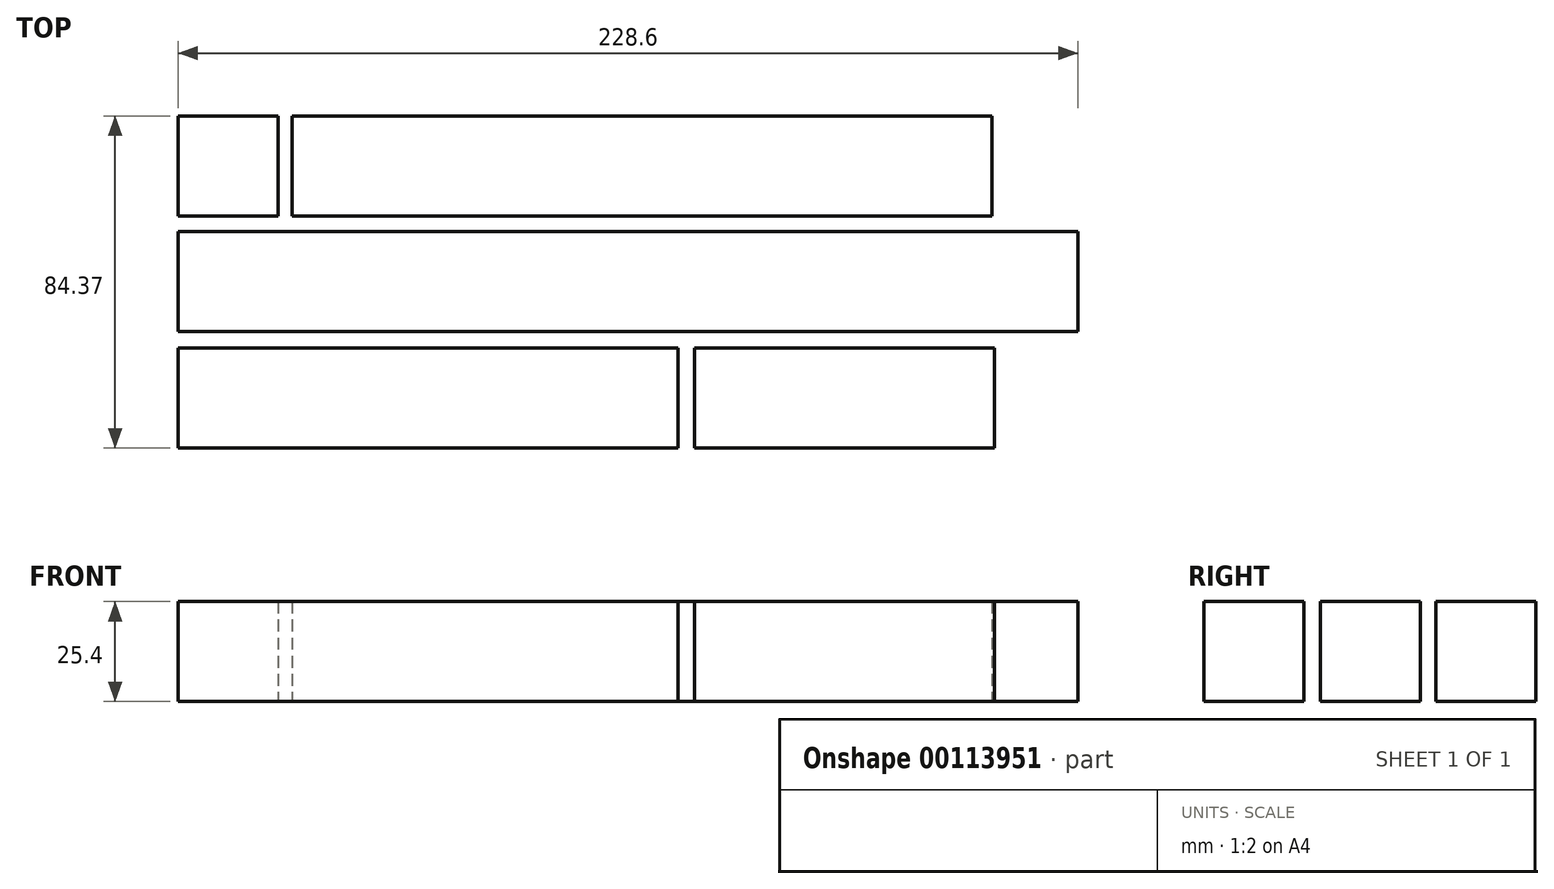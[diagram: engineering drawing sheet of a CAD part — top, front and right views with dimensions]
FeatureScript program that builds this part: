
annotation { "Feature Type Name" : "Feature", "Feature Type Description" : "" }
export const myFeature = defineFeature(function(context is Context, id is Id, definition is map)
    precondition{}
    {
        {
            var Q0;
            Q0=qCreatedBy(makeId("Top.planeOp"),FACE);
            var sketch = newSketch(context, id + "F0", { "sketchPlane" : qUnion([Q0])});
            skLineSegment(sketch, "E0.bottom", {"start": v(-116.9, 54.77) * mm, "end": v(-91.5, 54.77) * mm});
            skLineSegment(sketch, "E0.top", {"start": v(-116.9, 29.37) * mm, "end": v(-91.5, 29.37) * mm});
            skLineSegment(sketch, "E0.left", {"start": v(-116.9, 54.77) * mm, "end": v(-116.9, 29.37) * mm});
            skLineSegment(sketch, "E0.right", {"start": v(-91.5, 54.77) * mm, "end": v(-91.5, 29.37) * mm});
            skLineSegment(sketch, "E1.bottom", {"start": v(-116.9, 25.4) * mm, "end": v(111.7, 25.4) * mm});
            skLineSegment(sketch, "E1.top", {"start": v(-116.9, 0) * mm, "end": v(111.7, 0) * mm});
            skLineSegment(sketch, "E1.left", {"start": v(-116.9, 25.4) * mm, "end": v(-116.9, 0) * mm});
            skLineSegment(sketch, "E1.right", {"start": v(111.7, 25.4) * mm, "end": v(111.7, 0) * mm});
            skLineSegment(sketch, "E2.bottom", {"start": v(-87.91, 54.77) * mm, "end": v(89.89, 54.77) * mm});
            skLineSegment(sketch, "E2.top", {"start": v(-87.91, 29.37) * mm, "end": v(89.89, 29.37) * mm});
            skLineSegment(sketch, "E2.left", {"start": v(-87.91, 54.77) * mm, "end": v(-87.91, 29.37) * mm});
            skLineSegment(sketch, "E2.right", {"start": v(89.89, 54.77) * mm, "end": v(89.89, 29.37) * mm});
            skLineSegment(sketch, "E3.bottom", {"start": v(-116.9, -4.2) * mm, "end": v(10.1, -4.2) * mm});
            skLineSegment(sketch, "E3.top", {"start": v(-116.9, -29.6) * mm, "end": v(10.1, -29.6) * mm});
            skLineSegment(sketch, "E3.left", {"start": v(-116.9, -4.2) * mm, "end": v(-116.9, -29.6) * mm});
            skLineSegment(sketch, "E3.right", {"start": v(10.1, -4.2) * mm, "end": v(10.1, -29.6) * mm});
            skLineSegment(sketch, "E4.bottom", {"start": v(14.32, -4.2) * mm, "end": v(90.52, -4.2) * mm});
            skLineSegment(sketch, "E4.top", {"start": v(14.32, -29.6) * mm, "end": v(90.52, -29.6) * mm});
            skLineSegment(sketch, "E4.left", {"start": v(14.32, -4.2) * mm, "end": v(14.32, -29.6) * mm});
            skLineSegment(sketch, "E4.right", {"start": v(90.52, -4.2) * mm, "end": v(90.52, -29.6) * mm});
            skSolve(sketch);
        }
        {
            var Q0;
            Q0 = qSketchRegion(id + "F0", true);
            extrude(context, id + "F1", {"entities" : qUnion([Q0]), "depth" : 25.4 * mm});
        }
    });
